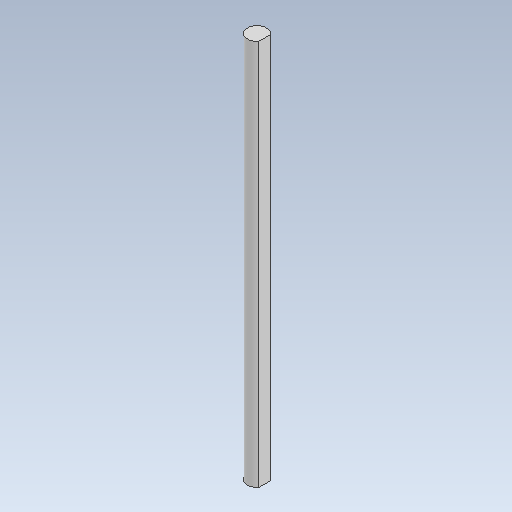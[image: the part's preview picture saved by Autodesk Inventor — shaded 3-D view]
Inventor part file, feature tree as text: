
AUTODESK INVENTOR PART (.ipt)
format: ipt  version: 2020 (Build 240168000, 168)  size: 92,672 bytes
history: native  units: in
note: dims shown in document units (in); Inventor stores cm internally (conversion verified against a paired STEP export)
features: extrude x1, sketch x1
ambient origin geometry x8: Origin, YZ Plane, XZ Plane, XY Plane, X Axis, Y Axis, Z Axis, Center Point
bodies: Solid1 (feature_tree)
feature tree (2):
  extrude  "Extrusion1"  Depth=5.0in TaperAngle=0.0deg
  sketch  "Sketch1"  dims[d0=0.25in d2=5.0in d3=0.0in]
